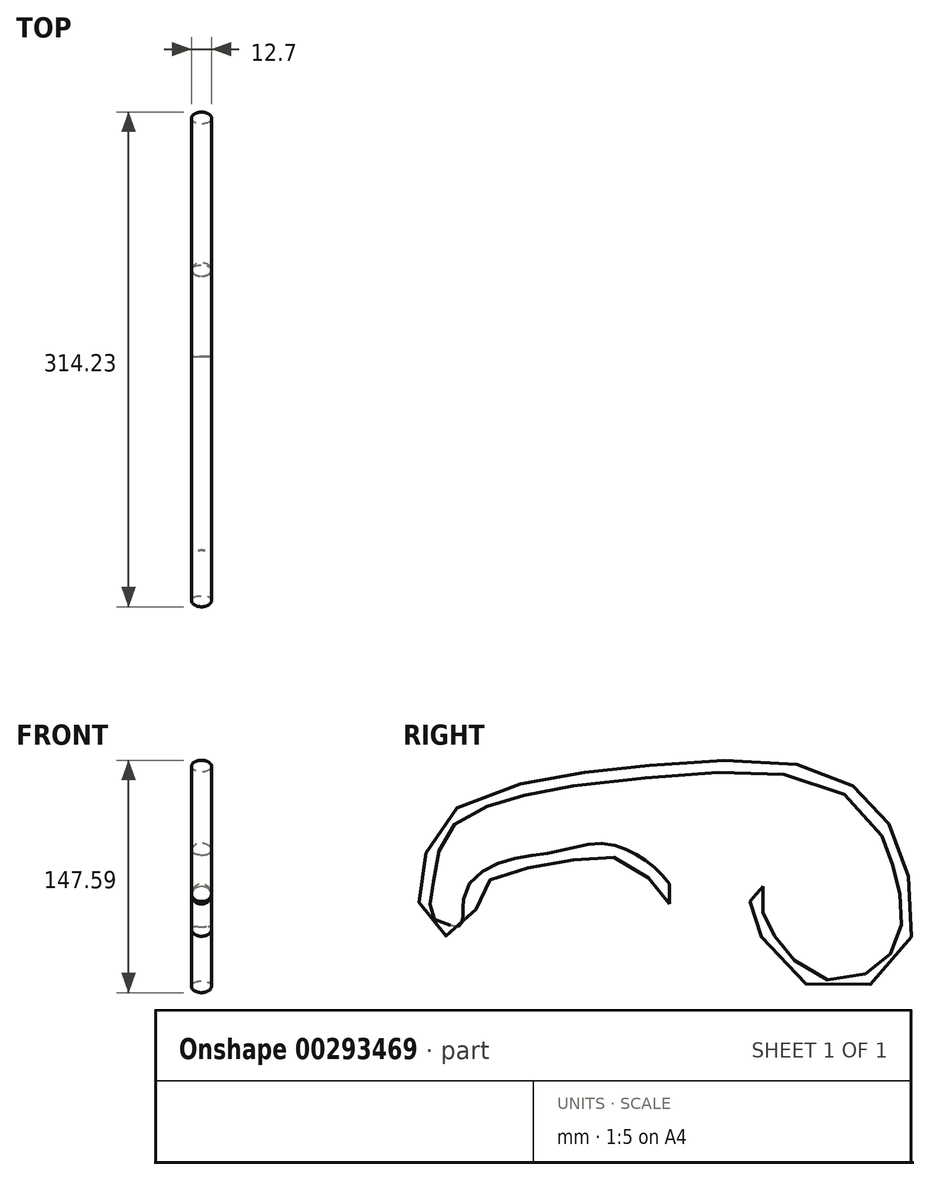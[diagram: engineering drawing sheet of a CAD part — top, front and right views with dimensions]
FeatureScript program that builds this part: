
annotation { "Feature Type Name" : "Feature", "Feature Type Description" : "" }
export const myFeature = defineFeature(function(context is Context, id is Id, definition is map)
    precondition{}
    {
        {
            var Q0;
            Q0=qCreatedBy(makeId("Right.planeOp"),FACE);
            var sketch = newSketch(context, id + "F0", { "sketchPlane" : qUnion([Q0])});
            skFitSpline(sketch, "E0", {"points": [v(0, 0) * mm, v(-12.8, 14.65) * mm, v(-40.25, 27.9) * mm, v(-71.5, 23.17) * mm, v(-105.57, 16.54) * mm, v(-125.46, 0) * mm, v(-130.19, -19.9) * mm, v(-150.54, -18.49) * mm, v(-153.38, 9.44) * mm, v(-140.13, 45.42) * mm, v(-78.12, 69.56) * mm, v(-9.95, 78.08) * mm, v(79.52, 78.56) * mm, v(126.85, 55.36) * mm, v(146.26, 17.02) * mm, v(146.26, -35.53) * mm, v(97.5, -57.3) * mm, v(57.27, -15.65) * mm, v(55.37, 0) * mm], "startDerivative": vector(-274.85, 376.45) * mm, "endDerivative": vector(30.92, 370.43) * mm});
            skSolve(sketch);
        }
        {
            var Q0;
            Q0=qCreatedBy(makeId("Front.planeOp"),FACE);
            var sketch = newSketch(context, id + "F1", { "sketchPlane" : qUnion([Q0])});
            skCircle(sketch, "E1", {"center": v(0, 0) * mm, "radius": 6.35 * mm});
            skSolve(sketch);
        }
        {
            var Q0;
            Q0=makeQuery(id+"F1.imprint","IMPRINT",FACE,{"disambiguationData":[TD([[makeQuery(id+"F1.imprint","IMPRINT",EDGE,{"derivedFrom":sQuery(id+"F1.wireOp",EDGE,"E1")}),1.0]])]});
            var Q1;
            Q1=sQuery(id+"F0.wireOp",EDGE,"E0");
            sweep(context, id + "F2", {"profiles" : qUnion([Q0]), "path" : qUnion([Q1])});
        }
    });
